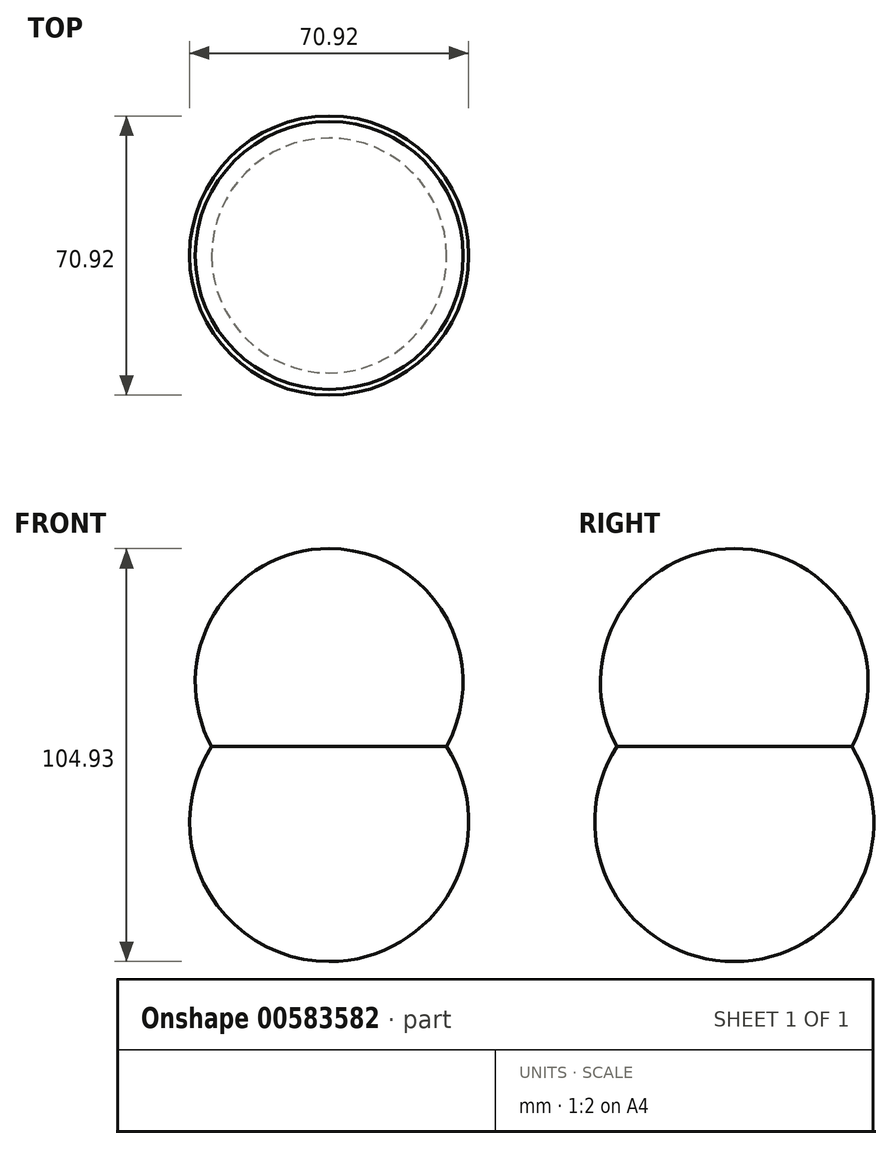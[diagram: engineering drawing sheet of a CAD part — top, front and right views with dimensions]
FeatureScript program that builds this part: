
annotation { "Feature Type Name" : "Feature", "Feature Type Description" : "" }
export const myFeature = defineFeature(function(context is Context, id is Id, definition is map)
    precondition{}
    {
        {
            var Q0;
            Q0=qCreatedBy(makeId("Front.planeOp"),FACE);
            var sketch = newSketch(context, id + "F0", { "sketchPlane" : qUnion([Q0])});
            skArc(sketch, "E0", {"start": v(0, -35.46) * mm, "mid": v(31.11, -17) * mm, "end": v(29.84, 19.15) * mm});
            skArc(sketch, "E1", {"start": v(29.84, 19.15) * mm, "mid": v(29.25, 52.8) * mm, "end": v(0, 69.47) * mm});
            skLineSegment(sketch, "E2", {"start": v(0, 35.46) * mm, "end": v(0, 76.68) * mm});
            skLineSegment(sketch, "E3", {"start": v(0, 76.68) * mm, "end": v(0, -44.6) * mm});
            skSolve(sketch);
        }
        {
            var Q0;
            {var subQ0=sQuery(id+"F0.wireOp",EDGE,"E0");Q0=makeQuery(id+"F0.imprint","IMPRINT",FACE,{"disambiguationData":[TD([[makeQuery(id+"F0.imprint","IMPRINT",EDGE,{"derivedFrom":subQ0}),1.0]])]});}
            var Q1;
            Q1=sQuery(id+"F0.wireOp",EDGE,"E3");
            revolve(context, id + "F1", {"entities" : qUnion([Q0]), "axis" : qUnion([Q1]), "revolveType" : RevolveType.FULL});
        }
    });
